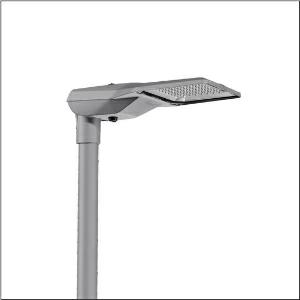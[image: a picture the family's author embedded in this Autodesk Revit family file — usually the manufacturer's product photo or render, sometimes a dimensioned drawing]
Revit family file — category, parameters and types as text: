
# Revit family: streetlight_sl_21_iq_midi___st1_0a_5xe3d21y08mb_afa7
name_source: partatom
category: Lighting Fixtures
units: mm (PartAtom-declared; Revit-internal decimal feet)

## family parameters
Cut with Voids When Loaded = No
Host = Face
Light Source = No
Part Type = Normal
Room Calculation Point = No
Round Connector Dimension = Use Diameter
Shared = No

## types (1)
- --- (1 x LED, 14710 lm, 129.3 W, 2200K)
    Apparent Load = 129 VA
    CIE Flux Codes = 37 72 97 100 100
    Color Rendering = 70
    Color Temperature = 2200K
    Default Elevation = 1800 mm
    Description = Streetlight SL 21 iQ midi, mast luminaire, primary light control with lens, of PMMA, primary optical cover: cover, of toughened safety glass, transparent, light distribution: ST1.0a, light emission: direct distribution, primary light characteristic: asymmetric, installation type: post-top, side-entry, LED, High Power LED, rated luminous flux: 14.710lm, luminous efficacy: 114lm/W, light colour: 722, colour temperature: 2200K, control gear: iQ-Street Remote, D4i with power reduction, control: pre-setting: logarithmic dimming characteristic, Street-Remote, Auto-Match, Temp-Guard, Lumen-Switch, Night-Set, Smart-Wire, Light-Fading, Desk-Remote (wireless, voltage-free reading and setting of iQ features in the workshop via application-optimized NFC function/RFID function), optimised constant luminous flux control (CLO 2.0), mains connection: 230..240V, AC, 50/60Hz, start of lifetime: 129W, end of service life: 142W, reduction: 56W, luminaire housing, of diecast aluminium, powder-coated, SITECO metallic grey (DB 702S), corrosivity category C5 high according to DIN EN ISO 12944, please order mast flange separately, inclination adjustable: 0°, 5°, 10°, 15°, sealing non-destructively replaceable, multi-level sealing system, length: 644mm, width: 335mm, height: 110mm, mast flange for spigot size: 42mm (side-entry): 5XC10008XM4, 60/48mm (side-entry/post-top): 5XC10108XM2, 76/60mm (side-entry/post-top): 5XC10108XM1, mounting height: 4..8m, Smart Interface below and above, protection rating (complete): IP66, insulation class (complete): insulation class II (safety insulation), certification: CE, ENEC, ENEC+, VDE, impact resistance: IK10, permissible operating ambient temperature for outdoor applications: -40..+50°C, standard-compliant lighting for roads and squares, packaging unit: 1 piece

Light Distribution: ST1.0a
    Height = 111 mm
    Lamp = 1 x LED
    Lamp Light Flux = 14710 lm
    Lamp Power = 129.3 W
    Lamp count = 1
    Length = 644 mm
    Luminous efficacy = 114 lm/W
    Manufacturer = Siteco
    ModVariant = No
    Model = 5XE3D21Y08MB
    Mounting Place = Pole
    Mounting Type = Pole top
    Number of Poles = 1
    OnlyDefault = Yes
    Power Factor = 1
    Product Name = Streetlight SL 21 iQ midi | ST1.0a
    Product group = mast luminaire | pylon top
    ProductGroupID = 6100
    Protection Class = Protection class II
    Protection Degree = IP 66
    RLX_Detail_Level = 1
    RLX_Emergency_Light_Flux = 0 lm
    RLX_Emergency_Type = 0
    RLX_Emergency_Type_DB = No
    RlxData = <blob elided: 91433 chars, md5=60ad7d9d>
    Socket = socket
    Standby Power = 0 W
    System Light Flux = 14710 lm
    System Power = 129 W
    Type Comments = factory setting: luminous flux: 100 % | dim-lin: 254 | 672 mA
    Type Image = l_1004304.jpg
    URL = http://relux.com
    VarID = @adj_116285
    Voltage = 0 V
    Weight = 0.00 kg
    Width = 336 mm

## geometry (parser evidence)
native form markers: Blend x4, Sweep x14
no freeform markers — native parametric forms only
